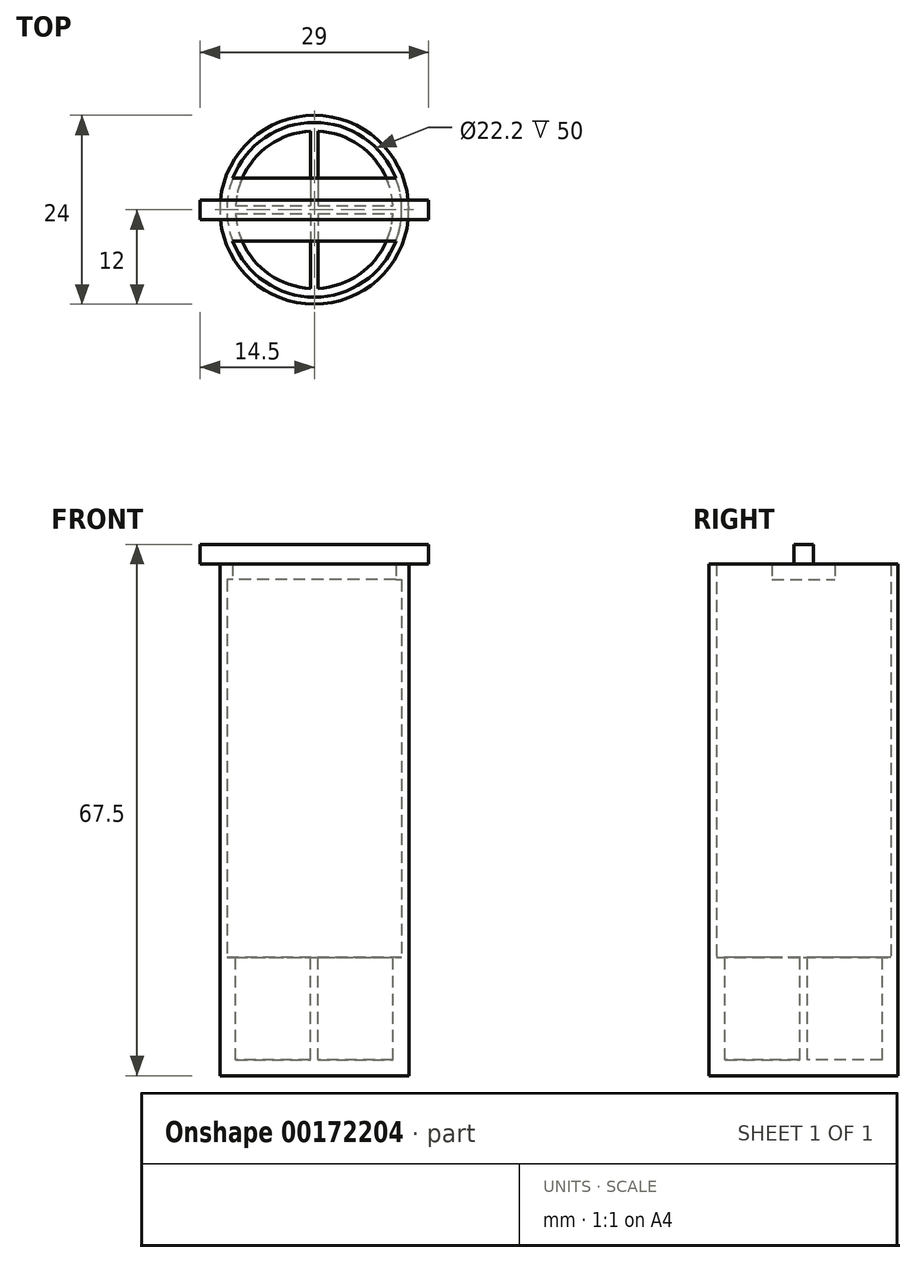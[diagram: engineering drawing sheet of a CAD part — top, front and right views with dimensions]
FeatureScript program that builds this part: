
annotation { "Feature Type Name" : "Feature", "Feature Type Description" : "" }
export const myFeature = defineFeature(function(context is Context, id is Id, definition is map)
    precondition{}
    {
        {
            var Q0;
            Q0=qCreatedBy(makeId("Top.planeOp"),FACE);
            var sketch = newSketch(context, id + "F0", { "sketchPlane" : qUnion([Q0])});
            skCircle(sketch, "E0", {"center": v(0, 0) * mm, "radius": 12 * mm});
            skSolve(sketch);
        }
        {
            var Q0;
            Q0=qSketchRegion(id+"F0",true);
            extrude(context, id + "F1", {"entities" : qUnion([Q0]), "depth" : 15 * mm});
        }
        {
            var Q0;
            Q0=makeQuery(id+"F1.opExtrude","CAP_FACE",FACE,{"disambiguationData":[OSD([sQuery(id+"F0.wireOp",EDGE,"E0")])],"isStart":false});
            var sketch = newSketch(context, id + "F2", { "sketchPlane" : qUnion([Q0])});
            skCircle(sketch, "E1", {"center": v(0, 0) * mm, "radius": 10 * mm});
            skLineSegment(sketch, "E2.bottom", {"start": v(0.5, 9.99) * mm, "end": v(-0.5, 9.99) * mm});
            skLineSegment(sketch, "E2.top", {"start": v(0.5, -9.99) * mm, "end": v(-0.5, -9.99) * mm});
            skLineSegment(sketch, "E2.left", {"start": v(0.5, 9.99) * mm, "end": v(0.5, -9.99) * mm});
            skLineSegment(sketch, "E2.right", {"start": v(-0.5, 9.99) * mm, "end": v(-0.5, -9.99) * mm});
            skLineSegment(sketch, "E3.bottom", {"start": v(-9.99, 0.5) * mm, "end": v(9.99, 0.5) * mm});
            skLineSegment(sketch, "E3.top", {"start": v(-9.99, -0.5) * mm, "end": v(9.99, -0.5) * mm});
            skLineSegment(sketch, "E3.left", {"start": v(-9.99, 0.5) * mm, "end": v(-9.99, -0.5) * mm});
            skLineSegment(sketch, "E3.right", {"start": v(9.99, 0.5) * mm, "end": v(9.99, -0.5) * mm});
            skSolve(sketch);
        }
        {
            var Q0;
            {var subQ0=sQuery(id+"F2.wireOp",EDGE,"E2.right");var subQ3=sQuery(id+"F2.wireOp",EDGE,"E3.bottom");var subQ5=makeQuery(id+"F2.imprint","INTERSECT",VERTEX,{"derivedFrom":[subQ0,subQ3]});Q0=makeQuery(id+"F2.imprint","IMPRINT",FACE,{"disambiguationData":[TD([[makeQuery(id+"F2.imprint","IMPRINT",EDGE,{"disambiguationData":[TD([[subQ5,1.0]])],"derivedFrom":subQ0}),-1.0]])]});}
            var Q1;
            {var subQ0=sQuery(id+"F2.wireOp",EDGE,"E2.left");var subQ3=sQuery(id+"F2.wireOp",EDGE,"E3.bottom");var subQ5=makeQuery(id+"F2.imprint","INTERSECT",VERTEX,{"derivedFrom":[subQ0,subQ3]});Q1=makeQuery(id+"F2.imprint","IMPRINT",FACE,{"disambiguationData":[TD([[makeQuery(id+"F2.imprint","IMPRINT",EDGE,{"disambiguationData":[TD([[subQ5,1.0]])],"derivedFrom":subQ0}),1.0]])]});}
            var Q2;
            {var subQ0=sQuery(id+"F2.wireOp",EDGE,"E2.left");var subQ3=sQuery(id+"F2.wireOp",EDGE,"E3.top");var subQ5=makeQuery(id+"F2.imprint","INTERSECT",VERTEX,{"derivedFrom":[subQ0,subQ3]});Q2=makeQuery(id+"F2.imprint","IMPRINT",FACE,{"disambiguationData":[TD([[makeQuery(id+"F2.imprint","IMPRINT",EDGE,{"disambiguationData":[TD([[subQ5,-1.0]])],"derivedFrom":subQ0}),1.0]])]});}
            var Q3;
            {var subQ0=sQuery(id+"F2.wireOp",EDGE,"E2.right");var subQ3=sQuery(id+"F2.wireOp",EDGE,"E3.top");var subQ5=makeQuery(id+"F2.imprint","INTERSECT",VERTEX,{"derivedFrom":[subQ0,subQ3]});Q3=makeQuery(id+"F2.imprint","IMPRINT",FACE,{"disambiguationData":[TD([[makeQuery(id+"F2.imprint","IMPRINT",EDGE,{"disambiguationData":[TD([[subQ5,-1.0]])],"derivedFrom":subQ0}),-1.0]])]});}
            extrude(context, id + "F3", {"entities" : qUnion([Q0, Q1, Q2, Q3]), "operationType" : NewBodyOperationType.REMOVE, "oppositeDirection" : true, "depth" : 13 * mm});
        }
        {
            var Q0;
            Q0=makeQuery(id+"F1.opExtrude","CAP_FACE",FACE,{"disambiguationData":[OSD([sQuery(id+"F0.wireOp",EDGE,"E0")])],"isStart":false});
            var sketch = newSketch(context, id + "F4", { "sketchPlane" : qUnion([Q0])});
            skCircle(sketch, "E4", {"center": v(0, 0) * mm, "radius": 12 * mm});
            skCircle(sketch, "E5", {"center": v(0, 0) * mm, "radius": 11.1 * mm});
            skSolve(sketch);
        }
        {
            var Q0;
            Q0=qSketchRegion(id+"F4",true);
            extrude(context, id + "F5", {"entities" : qUnion([Q0]), "operationType" : NewBodyOperationType.ADD, "depth" : 50 * mm});
        }
        {
            var Q0;
            Q0=makeQuery(id+"F5.opExtrude","CAP_FACE",FACE,{"disambiguationData":[OSD([sQuery(id+"F4.wireOp",EDGE,"E4"),sQuery(id+"F4.wireOp",EDGE,"E5")])],"isStart":false});
            var sketch = newSketch(context, id + "F6", { "sketchPlane" : qUnion([Q0])});
            skLineSegment(sketch, "E6.bottom", {"start": v(14.81, -4) * mm, "end": v(-14.81, -4) * mm});
            skLineSegment(sketch, "E6.top", {"start": v(14.81, 4) * mm, "end": v(-14.81, 4) * mm});
            skLineSegment(sketch, "E6.left", {"start": v(14.81, -4) * mm, "end": v(14.81, 4) * mm});
            skLineSegment(sketch, "E6.right", {"start": v(-14.81, -4) * mm, "end": v(-14.81, 4) * mm});
            skPoint(sketch, "E6.middle", {"position": v(0, 0) * mm});
            skLineSegment(sketch, "E7.bottom", {"start": v(-14.81, 4) * mm, "end": v(15.46, 4) * mm});
            skLineSegment(sketch, "E7.top", {"start": v(-14.81, 13.03) * mm, "end": v(15.46, 13.03) * mm});
            skLineSegment(sketch, "E7.left", {"start": v(-14.81, 4) * mm, "end": v(-14.81, 13.03) * mm});
            skLineSegment(sketch, "E7.right", {"start": v(15.46, 4) * mm, "end": v(15.46, 13.03) * mm});
            skLineSegment(sketch, "E8.bottom", {"start": v(-14.81, -4) * mm, "end": v(14.97, -4) * mm});
            skLineSegment(sketch, "E8.top", {"start": v(-14.81, -14.85) * mm, "end": v(14.97, -14.85) * mm});
            skLineSegment(sketch, "E8.left", {"start": v(-14.81, -4) * mm, "end": v(-14.81, -14.85) * mm});
            skLineSegment(sketch, "E8.right", {"start": v(14.97, -4) * mm, "end": v(14.97, -14.85) * mm});
            skSolve(sketch);
        }
        {
            var Q0;
            {var subQ0=sQuery(id+"F6.wireOp",EDGE,"E7.bottom");var subQ1=makeQuery(id+"F5.opExtrude","CAP_EDGE",EDGE,{"disambiguationData":[OSD([sQuery(id+"F4.wireOp",EDGE,"E5")])],"isStart":false});var subQ2=makeQuery(id+"F6.imprint","INTERSECT",VERTEX,{"disambiguationData":[OD(0.0)],"derivedFrom":[subQ1,subQ0]});Q0=makeQuery(id+"F6.imprint","IMPRINT",FACE,{"disambiguationData":[TD([[makeQuery(id+"F6.imprint","IMPRINT",EDGE,{"disambiguationData":[TD([[subQ2,-1.0]])],"derivedFrom":subQ0}),1.0]])]});}
            var Q1;
            {var subQ0=sQuery(id+"F6.wireOp",EDGE,"E8.bottom");var subQ1=makeQuery(id+"F5.opExtrude","CAP_EDGE",EDGE,{"disambiguationData":[OSD([sQuery(id+"F4.wireOp",EDGE,"E5")])],"isStart":false});var subQ2=makeQuery(id+"F6.imprint","INTERSECT",VERTEX,{"disambiguationData":[OD(0.0)],"derivedFrom":[subQ1,subQ0]});Q1=makeQuery(id+"F6.imprint","IMPRINT",FACE,{"disambiguationData":[TD([[makeQuery(id+"F6.imprint","IMPRINT",EDGE,{"disambiguationData":[TD([[subQ2,-1.0]])],"derivedFrom":subQ0}),-1.0]])]});}
            var Q2;
            Q2=makeQuery(id+"F6.imprint","IMPRINT",FACE,{"disambiguationData":[TD([[makeQuery(id+"F6.imprint","IMPRINT",EDGE,{"derivedFrom":sQuery(id+"F6.wireOp",EDGE,"E7.top")}),-1.0]])]});
            var Q3;
            Q3=makeQuery(id+"F6.imprint","IMPRINT",FACE,{"disambiguationData":[TD([[makeQuery(id+"F6.imprint","IMPRINT",EDGE,{"derivedFrom":sQuery(id+"F6.wireOp",EDGE,"E8.top")}),1.0]])]});
            var Q4;
            {var subQ0=sQuery(id+"F6.wireOp",EDGE,"E7.bottom");var subQ1=makeQuery(id+"F5.opExtrude","CAP_EDGE",EDGE,{"disambiguationData":[OSD([sQuery(id+"F4.wireOp",EDGE,"E4")])],"isStart":false});var subQ2=makeQuery(id+"F6.imprint","INTERSECT",VERTEX,{"disambiguationData":[OD(0.0)],"derivedFrom":[subQ1,subQ0]});Q4=makeQuery(id+"F6.imprint","IMPRINT",FACE,{"disambiguationData":[TD([[makeQuery(id+"F6.imprint","IMPRINT",EDGE,{"disambiguationData":[TD([[subQ2,-1.0]])],"derivedFrom":subQ0}),1.0]])]});}
            var Q5;
            {var subQ0=sQuery(id+"F6.wireOp",EDGE,"E8.bottom");var subQ1=makeQuery(id+"F5.opExtrude","CAP_EDGE",EDGE,{"disambiguationData":[OSD([sQuery(id+"F4.wireOp",EDGE,"E4")])],"isStart":false});var subQ2=makeQuery(id+"F6.imprint","INTERSECT",VERTEX,{"disambiguationData":[OD(0.0)],"derivedFrom":[subQ1,subQ0]});Q5=makeQuery(id+"F6.imprint","IMPRINT",FACE,{"disambiguationData":[TD([[makeQuery(id+"F6.imprint","IMPRINT",EDGE,{"disambiguationData":[TD([[subQ2,-1.0]])],"derivedFrom":subQ0}),-1.0]])]});}
            extrude(context, id + "F7", {"entities" : qUnion([Q0, Q1, Q2, Q3, Q4, Q5]), "operationType" : NewBodyOperationType.REMOVE, "oppositeDirection" : true, "depth" : 50 * mm});
        }
        {
            var Q0;
            Q0=makeQuery(id+"F7.boolean.opBoolean","SPLIT",FACE,{"disambiguationData":[OD(1.0)],"derivedFrom":makeQuery(id+"F5.opExtrude","CAP_FACE",FACE,{"disambiguationData":[OSD([sQuery(id+"F4.wireOp",EDGE,"E4"),sQuery(id+"F4.wireOp",EDGE,"E5")])],"isStart":false})});
            var sketch = newSketch(context, id + "F8", { "sketchPlane" : qUnion([Q0])});
            skLineSegment(sketch, "E9.bottom", {"start": v(11.31, 4) * mm, "end": v(-11.31, 4) * mm});
            skLineSegment(sketch, "E9.top", {"start": v(11.31, -4) * mm, "end": v(-11.31, -4) * mm});
            skLineSegment(sketch, "E9.left", {"start": v(11.31, 4) * mm, "end": v(11.31, -4) * mm});
            skLineSegment(sketch, "E9.right", {"start": v(-11.31, 4) * mm, "end": v(-11.31, -4) * mm});
            skPoint(sketch, "E9.middle", {"position": v(0, 0) * mm});
            skSolve(sketch);
        }
        {
            var Q0;
            Q0=qSketchRegion(id+"F8",true);
            extrude(context, id + "F9", {"entities" : qUnion([Q0]), "operationType" : NewBodyOperationType.ADD, "oppositeDirection" : true, "depth" : 2 * mm});
        }
        {
            var Q0;
            {var subQ0=makeQuery(id+"F5.opExtrude","CAP_FACE",FACE,{"disambiguationData":[OSD([sQuery(id+"F4.wireOp",EDGE,"E4"),sQuery(id+"F4.wireOp",EDGE,"E5")])],"isStart":false});Q0=makeQuery(id+"F9.boolean.opBoolean","MERGE",FACE,{"derivedFrom":[makeQuery(id+"F7.boolean.opBoolean","SPLIT",FACE,{"disambiguationData":[OD(0.0)],"derivedFrom":subQ0}),makeQuery(id+"F7.boolean.opBoolean","SPLIT",FACE,{"disambiguationData":[OD(1.0)],"derivedFrom":subQ0}),makeQuery(id+"F9.opExtrude","CAP_FACE",FACE,{"disambiguationData":[OSD([sQuery(id+"F8.wireOp",EDGE,"E9.bottom"),sQuery(id+"F8.wireOp",EDGE,"E9.top"),sQuery(id+"F8.wireOp",EDGE,"E9.left"),sQuery(id+"F8.wireOp",EDGE,"E9.right")])],"isStart":true})]});}
            var sketch = newSketch(context, id + "F10", { "sketchPlane" : qUnion([Q0])});
            skLineSegment(sketch, "E10.bottom", {"start": v(14.5, -1.25) * mm, "end": v(-14.5, -1.25) * mm});
            skLineSegment(sketch, "E10.top", {"start": v(14.5, 1.25) * mm, "end": v(-14.5, 1.25) * mm});
            skLineSegment(sketch, "E10.left", {"start": v(14.5, -1.25) * mm, "end": v(14.5, 1.25) * mm});
            skLineSegment(sketch, "E10.right", {"start": v(-14.5, -1.25) * mm, "end": v(-14.5, 1.25) * mm});
            skPoint(sketch, "E10.middle", {"position": v(0, 0) * mm});
            skSolve(sketch);
        }
        {
            var Q0;
            Q0=qSketchRegion(id+"F10",true);
            extrude(context, id + "F11", {"entities" : qUnion([Q0]), "operationType" : NewBodyOperationType.ADD, "depth" : 2.5 * mm});
        }
    });
